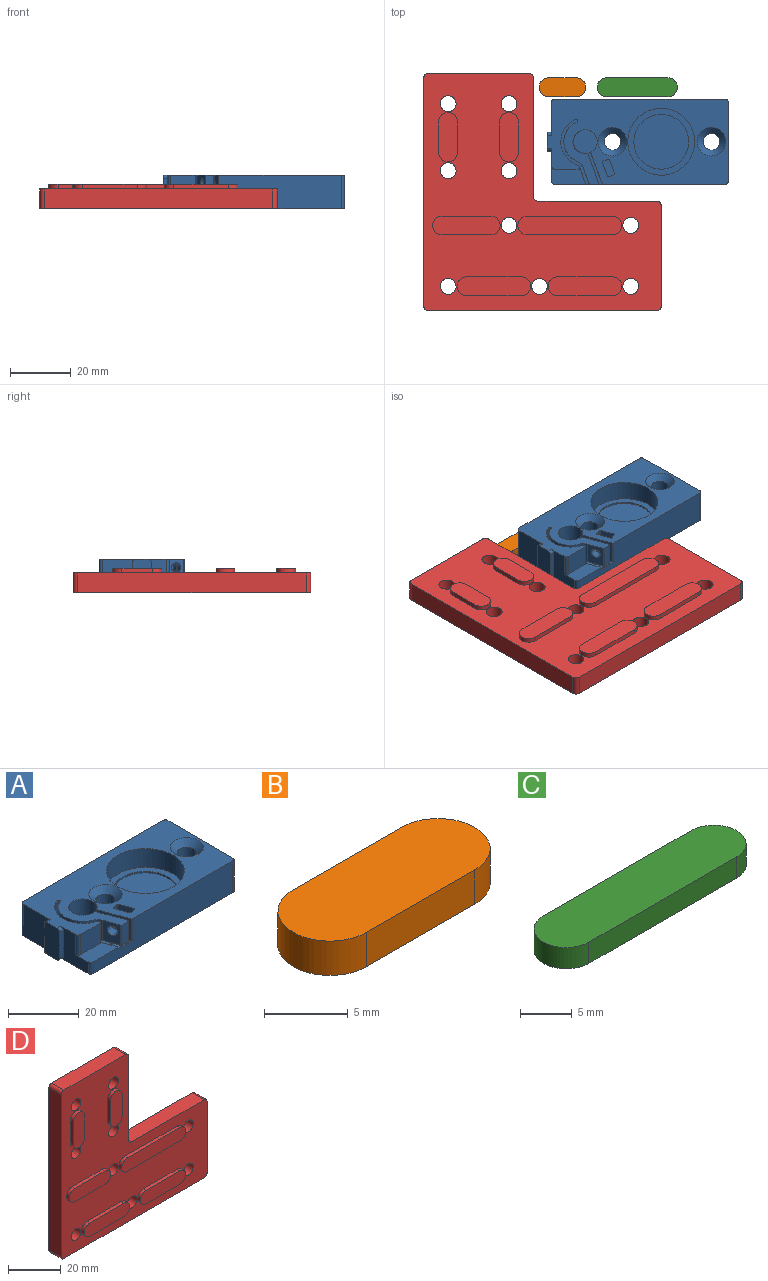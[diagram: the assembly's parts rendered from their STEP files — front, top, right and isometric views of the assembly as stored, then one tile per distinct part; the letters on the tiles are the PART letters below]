
ASSEMBLY  parts=4 mates=3
PART A: 89 faces, bbox 59.5x28x11 mm
  f0: plane 0.33x0.24mm, normal (0,0,-1), area 0mm2, adj f13,f29,f73
  f1: plane 59.5x28mm, normal (0,0,-1), area 1340.5mm2, adj f2,f24,f25,f26,f27,f44,f46,f53
  f2: plane 11x10.9mm, normal (-1,0,0), area 74.3mm2, adj f1,f12,f41,f51,f65,f66,f68,f69
  f3: cylinder r=0.3mm len=7.5mm, axis (0,0,1), area 3.6mm2, adj f4,f12,f21,f43
  f4: cylinder r=8mm len=14.77mm, axis (0,0,1), area 141.2mm2, adj f3,f5,f12,f43
  f5: cylinder r=3mm len=7.5mm, axis (0,0,1), area 13.8mm2, adj f4,f9,f12,f22,f43
  f6: cylinder r=0.3mm len=7.5mm, axis (0,0,1), area 2.7mm2, adj f7,f12,f27,f43
  f7: plane 10.43x7.5mm, normal (-0.94,-0.34,0), area 73.8mm2, adj f6,f8,f12,f29,f39,f42,f43
  f8: cylinder r=3.8mm len=7.37mm, axis (0,0,1), area 6.2mm2, adj f7,f21,f42,f43
  f9: plane 5.07x1.85mm, normal (0.94,0.34,0), area 2.7mm2, adj f5,f10,f22,f41,f43
  f10: cylinder r=0.3mm len=0.5mm, axis (0,0,1), area 0.3mm2, adj f9,f27,f41,f43
  f11: plane 20.85x11.42mm, normal (0,0,-1), area 68.7mm2, adj f13,f14,f15,f16,f17,f18,f19,f20
  f12: plane 59.5x28mm, normal (0,0,1), area 957.2mm2, adj f2,f3,f4,f5,f6,f7,f13,f14
  f13: plane 9.7x7mm, normal (0.94,0.34,0), area 64.2mm2, adj f0,f11,f12,f14,f29,f40
  f14: cylinder r=0.3mm len=7.5mm, axis (0,0,1), area 5mm2, adj f11,f12,f13,f15,f43
  f15: plane 7x2.55mm, normal (0,-1,0), area 17.9mm2, adj f11,f12,f14,f16
  f16: cylinder r=0.3mm len=7mm, axis (0,0,1), area 2.6mm2, adj f11,f12,f15,f17
  f17: plane 7x5.46mm, normal (-0.94,-0.34,0), area 32.7mm2, adj f11,f12,f16,f18,f40
  f18: cylinder r=3mm len=7mm, axis (0,0,1), area 18.1mm2, adj f11,f12,f17,f19
  f19: cylinder r=7mm len=13.03mm, axis (0,0,1), area 117.3mm2, adj f11,f12,f18,f20,f75
  f20: cylinder r=0.3mm len=7mm, axis (0,0,1), area 3.2mm2, adj f11,f12,f19,f21
  f21: plane 7.5x3.66mm, normal (-0.94,-0.34,0), area 4.7mm2, adj f3,f8,f11,f12,f20,f42,f43
  f22: cylinder r=0.3mm len=7mm, axis (0,0,1), area 4.5mm2, adj f5,f9,f12,f23,f41
  f23: plane 8x7mm, normal (0,-1,0), area 56mm2, adj f12,f22,f41,f69
  f24: plane 11x10.9mm, normal (-1,0,0), area 109.3mm2, adj f1,f12,f52,f64,f67,f70
  f25: plane 56x11mm, normal (0,1,0), area 616mm2, adj f1,f12,f70,f71
  f26: plane 26x11mm, normal (1,0,0), area 286mm2, adj f1,f12,f71,f72
  f27: plane 56x11mm, normal (0,-1,0), area 502.1mm2, adj f1,f6,f10,f12,f41,f43,f68,f72
  f28: cylinder r=11mm len=22mm, axis (0,0,1), area 449.2mm2, adj f12,f49
  f29: cylinder r=4mm len=8mm, axis (0,0,1), area 168.9mm2, adj f0,f7,f11,f12,f13,f42
  f30: plane 5.5x4.6mm, normal (-0.94,-0.34,0), area 27mm2, adj f12,f31,f37,f38
  f31: cylinder r=0.3mm len=5.5mm, axis (0,0,1), area 2.6mm2, adj f12,f30,f32,f38
  f32: plane 5.5x1.79mm, normal (-0.34,0.94,0), area 10.4mm2, adj f12,f31,f33,f38
  f33: cylinder r=0.3mm len=5.5mm, axis (0,0,1), area 2.6mm2, adj f12,f32,f34,f38
  f34: plane 5.5x4.6mm, normal (0.94,0.34,0), area 18.9mm2, adj f12,f33,f35,f38,f39
  f35: cylinder r=0.3mm len=5.5mm, axis (0,0,1), area 2.6mm2, adj f12,f34,f36,f38
  f36: plane 5.5x1.79mm, normal (0.34,-0.94,0), area 10.4mm2, adj f12,f35,f37,f38
  f37: cylinder r=0.3mm len=5.5mm, axis (0,0,1), area 2.6mm2, adj f12,f30,f36,f38
  f38: plane 5.85x4.06mm, normal (0,0,1), area 13.7mm2, adj f30,f31,f32,f33,f34,f35,f36,f37
  f39: cylinder r=1.6mm len=3.86mm, axis (0.94,0.34,0), area 25.1mm2, adj f7,f34
  f40: cylinder r=1.6mm len=4.03mm, axis (0.94,0.34,0), area 30.2mm2, adj f13,f17
  f41: plane 11.11x6mm, normal (0,0,1), area 51.6mm2, adj f2,f9,f10,f22,f23,f27,f68,f69
  f42: plane 7.8x7.8mm, normal (0,0,1), area 47.7mm2, adj f7,f8,f21,f29
  f43: plane 21.43x13.84mm, normal (0,0,1), area 108.9mm2, adj f3,f4,f5,f6,f7,f8,f9,f10
  f44: cylinder r=2.75mm len=9.05mm, axis (0,0,1), area 156.4mm2, adj f1,f45
  f45: cone r=2.75mm half-angle=45deg, axis (0,0,1), area 64.5mm2, adj f12,f44
  f46: cylinder r=2.75mm len=9.05mm, axis (0,0,1), area 156.4mm2, adj f1,f47
  f47: cone r=2.75mm half-angle=45deg, axis (0,0,1), area 64.5mm2, adj f12,f46
  f48: cylinder r=9mm len=18mm, axis (0,0,-1), area 28.3mm2, adj f49,f50
  f49: plane 22x22mm, normal (0,0,1), area 125.7mm2, adj f28,f48
  f50: plane 18x18mm, normal (0,0,1), area 254.5mm2, adj f48
  f51: plane 9x1.5mm, normal (0,-1,0), area 13.5mm2, adj f2,f53,f65,f66
  f52: plane 9x1.5mm, normal (0,1,0), area 13.5mm2, adj f24,f53,f64,f67
  f53: plane 11x6.2mm, normal (-1,0,0), area 67.3mm2, adj f1,f12,f51,f52,f64,f65,f66,f67
  f54: cylinder r=3.1mm len=6.2mm, axis (0,0,-1), area 14.6mm2, adj f1,f55,f57,f58
  f55: plane 9.1x1.5mm, normal (0,1,0), area 13.7mm2, adj f1,f54,f56,f58
  f56: cylinder r=3.1mm len=6.2mm, axis (0,0,-1), area 14.6mm2, adj f1,f55,f57,f58
  f57: plane 9.1x1.5mm, normal (0,-1,0), area 13.7mm2, adj f1,f54,f56,f58
  f58: plane 15.3x6.2mm, normal (0,0,-1), area 86.6mm2, adj f54,f55,f56,f57
  f59: cylinder r=3.1mm len=6.2mm, axis (0,0,-1), area 14.6mm2, adj f1,f60,f62,f63
  f60: plane 20.1x1.5mm, normal (0,1,0), area 30.1mm2, adj f1,f59,f61,f63
  f61: cylinder r=3.1mm len=6.2mm, axis (0,0,-1), area 14.6mm2, adj f1,f60,f62,f63
  f62: plane 20.1x1.5mm, normal (0,-1,0), area 30.1mm2, adj f1,f59,f61,f63
  f63: plane 26.3x6.2mm, normal (0,0,-1), area 154.8mm2, adj f59,f60,f61,f62
  f64: cylinder r=1mm len=1.5mm, axis (1,0,0), area 2.4mm2, adj f12,f24,f52,f53
  f65: cylinder r=1mm len=1.5mm, axis (-1,0,0), area 2.4mm2, adj f2,f12,f51,f53
  f66: cylinder r=1mm len=1.5mm, axis (-1,0,0), area 2.4mm2, adj f1,f2,f51,f53
  f67: cylinder r=1mm len=1.5mm, axis (1,0,0), area 2.4mm2, adj f1,f24,f52,f53
  f68: cylinder r=1mm len=4mm, axis (0,0,1), area 6.3mm2, adj f1,f2,f27,f41
  f69: cylinder r=1mm len=7mm, axis (0,0,-1), area 11mm2, adj f2,f12,f23,f41
  f70: cylinder r=1mm len=11mm, axis (0,0,-1), area 17.3mm2, adj f1,f12,f24,f25
  f71: cylinder r=1mm len=11mm, axis (0,0,1), area 17.3mm2, adj f1,f12,f25,f26
  f72: cylinder r=1mm len=11mm, axis (0,0,-1), area 17.3mm2, adj f1,f12,f26,f27
  f73: cylinder r=0.3mm len=0.6mm, axis (0,0,1), area 0.9mm2, adj f0,f11,f43
  f74: cylinder r=0.3mm len=0.6mm, axis (0,0,1), area 0.9mm2, adj f11,f43,f75
  f75: plane 0.12x0.05mm, normal (0,0,1), area 0mm2, adj f19,f74
  f76: cylinder r=0.3mm len=0.6mm, axis (0,0,1), area 0.9mm2, adj f11,f43
  f77: cylinder r=0.3mm len=0.6mm, axis (0,0,1), area 0.9mm2, adj f11,f43
  f78: cylinder r=0.3mm len=0.6mm, axis (0,0,1), area 0.9mm2, adj f11,f43
  f79: cylinder r=0.3mm len=0.6mm, axis (0,0,1), area 0.9mm2, adj f11,f43
  f80: cylinder r=0.3mm len=0.6mm, axis (0,0,1), area 0.9mm2, adj f11,f43
  f81: cylinder r=0.3mm len=0.6mm, axis (0,0,1), area 0.9mm2, adj f11,f43
  f82: cylinder r=0.3mm len=0.6mm, axis (0,0,1), area 0.9mm2, adj f11,f43
  f83: cylinder r=0.3mm len=0.6mm, axis (0,0,1), area 0.9mm2, adj f11,f43
  f84: cylinder r=0.3mm len=0.6mm, axis (0,0,1), area 0.9mm2, adj f11,f43
  f85: cylinder r=0.3mm len=0.6mm, axis (0,0,1), area 0.9mm2, adj f11,f43
  f86: cylinder r=0.3mm len=0.6mm, axis (0,0,1), area 0.9mm2, adj f11,f43
  f87: cylinder r=0.3mm len=0.6mm, axis (0,0,1), area 0.9mm2, adj f11,f43
  f88: cylinder r=0.3mm len=0.6mm, axis (0,0,1), area 0.9mm2, adj f11,f43
PART B: 6 faces, bbox 15.3x6.2x2.5 mm
  f0: cylinder r=3.1mm len=6.2mm, axis (0,0,1), area 24.3mm2, adj f1,f3,f4,f5
  f1: plane 9.1x2.5mm, normal (0,-1,0), area 22.8mm2, adj f0,f2,f4,f5
  f2: cylinder r=3.1mm len=6.2mm, axis (0,0,1), area 24.3mm2, adj f1,f3,f4,f5
  f3: plane 9.1x2.5mm, normal (0,1,0), area 22.8mm2, adj f0,f2,f4,f5
  f4: plane 15.3x6.2mm, normal (0,0,-1), area 86.6mm2, adj f0,f1,f2,f3
  f5: plane 15.3x6.2mm, normal (0,0,1), area 86.6mm2, adj f0,f1,f2,f3
PART C: 6 faces, bbox 26.3x6.2x2.5 mm
  f0: cylinder r=3.1mm len=6.2mm, axis (0,0,1), area 24.3mm2, adj f1,f3,f4,f5
  f1: plane 20.1x2.5mm, normal (0,-1,0), area 50.3mm2, adj f0,f2,f4,f5
  f2: cylinder r=3.1mm len=6.2mm, axis (0,0,1), area 24.3mm2, adj f1,f3,f4,f5
  f3: plane 20.1x2.5mm, normal (0,1,0), area 50.3mm2, adj f0,f2,f4,f5
  f4: plane 26.3x6.2mm, normal (0,0,-1), area 154.8mm2, adj f0,f1,f2,f3
  f5: plane 26.3x6.2mm, normal (0,0,1), area 154.8mm2, adj f0,f1,f2,f3
PART D: 53 faces, bbox 78x8x78 mm
  f0: plane 39x6.5mm, normal (0,0,1), area 253.5mm2, adj f6,f7,f47,f52
  f1: plane 39x6.5mm, normal (1,0,0), area 253.5mm2, adj f6,f7,f47,f48
  f2: plane 33x6.5mm, normal (0,0,1), area 214.5mm2, adj f6,f7,f48,f49
  f3: plane 75x6.5mm, normal (-1,0,0), area 487.5mm2, adj f6,f7,f49,f50
  f4: plane 75x6.5mm, normal (0,0,-1), area 487.5mm2, adj f6,f7,f50,f51
  f5: plane 33x6.5mm, normal (1,0,0), area 214.5mm2, adj f6,f7,f51,f52
  f6: plane 78x78mm, normal (0,-1,0), area 3325.8mm2, adj f0,f1,f2,f3,f4,f5,f8,f9
  f7: plane 78x78mm, normal (0,1,0), area 4126.9mm2, adj f0,f1,f2,f3,f4,f5,f8,f9
  f8: cylinder r=2.6mm len=6.5mm, axis (0,1,0), area 106.2mm2, adj f6,f7
  f9: cylinder r=2.6mm len=6.5mm, axis (0,1,0), area 106.2mm2, adj f6,f7
  f10: cylinder r=2.6mm len=6.5mm, axis (0,1,0), area 106.2mm2, adj f6,f7
  f11: cylinder r=2.6mm len=6.5mm, axis (0,1,0), area 106.2mm2, adj f6,f7
  f12: cylinder r=2.6mm len=6.5mm, axis (0,1,0), area 106.2mm2, adj f6,f7
  f13: cylinder r=2.6mm len=6.5mm, axis (0,1,0), area 106.2mm2, adj f6,f7
  f14: cylinder r=2.6mm len=6.5mm, axis (0,1,0), area 106.2mm2, adj f6,f7
  f15: cylinder r=2.6mm len=6.5mm, axis (0,1,0), area 106.2mm2, adj f6,f7
  f16: cylinder r=2.6mm len=6.5mm, axis (0,1,0), area 106.2mm2, adj f6,f7
  f17: cylinder r=3.1mm len=6.2mm, axis (0,1,0), area 14.6mm2, adj f6,f18,f20,f21
  f18: plane 28x1.5mm, normal (0,0,1), area 42mm2, adj f6,f17,f19,f21
  f19: cylinder r=3.1mm len=6.2mm, axis (0,1,0), area 14.6mm2, adj f6,f18,f20,f21
  f20: plane 28x1.5mm, normal (0,0,-1), area 42mm2, adj f6,f17,f19,f21
  f21: plane 34.2x6.2mm, normal (0,-1,0), area 203.8mm2, adj f17,f18,f19,f20
  f22: cylinder r=3.1mm len=6.2mm, axis (0,1,0), area 14.6mm2, adj f6,f23,f25,f26
  f23: plane 18x1.5mm, normal (0,0,1), area 27mm2, adj f6,f22,f24,f26
  f24: cylinder r=3.1mm len=6.2mm, axis (0,1,0), area 14.6mm2, adj f6,f23,f25,f26
  f25: plane 18x1.5mm, normal (0,0,-1), area 27mm2, adj f6,f22,f24,f26
  f26: plane 24.2x6.2mm, normal (0,-1,0), area 141.8mm2, adj f22,f23,f24,f25
  f27: cylinder r=3.1mm len=6.2mm, axis (0,1,0), area 14.6mm2, adj f6,f28,f30,f31
  f28: plane 18x1.5mm, normal (0,0,1), area 27mm2, adj f6,f27,f29,f31
  f29: cylinder r=3.1mm len=6.2mm, axis (0,1,0), area 14.6mm2, adj f6,f28,f30,f31
  f30: plane 18x1.5mm, normal (0,0,-1), area 27mm2, adj f6,f27,f29,f31
  f31: plane 24.2x6.2mm, normal (0,-1,0), area 141.8mm2, adj f27,f28,f29,f30
  f32: cylinder r=3.1mm len=6.2mm, axis (0,1,0), area 14.6mm2, adj f6,f33,f35,f36
  f33: plane 10x1.5mm, normal (1,0,0), area 15mm2, adj f6,f32,f34,f36
  f34: cylinder r=3.1mm len=6.2mm, axis (0,1,0), area 14.6mm2, adj f6,f33,f35,f36
  f35: plane 10x1.5mm, normal (-1,0,0), area 15mm2, adj f6,f32,f34,f36
  f36: plane 16.2x6.2mm, normal (0,-1,0), area 92.2mm2, adj f32,f33,f34,f35
  f37: cylinder r=3.1mm len=6.2mm, axis (0,1,0), area 14.6mm2, adj f6,f38,f40,f41
  f38: plane 10x1.5mm, normal (1,0,0), area 15mm2, adj f6,f37,f39,f41
  f39: cylinder r=3.1mm len=6.2mm, axis (0,1,0), area 14.6mm2, adj f6,f38,f40,f41
  f40: plane 10x1.5mm, normal (-1,0,0), area 15mm2, adj f6,f37,f39,f41
  f41: plane 16.2x6.2mm, normal (0,-1,0), area 92.2mm2, adj f37,f38,f39,f40
  f42: cylinder r=3.1mm len=6.2mm, axis (0,1,0), area 14.6mm2, adj f6,f43,f45,f46
  f43: plane 16x1.5mm, normal (0,0,1), area 24mm2, adj f6,f42,f44,f46
  f44: cylinder r=3.1mm len=6.2mm, axis (0,1,0), area 14.6mm2, adj f6,f43,f45,f46
  f45: plane 16x1.5mm, normal (0,0,-1), area 24mm2, adj f6,f42,f44,f46
  f46: plane 22.2x6.2mm, normal (0,-1,0), area 129.4mm2, adj f42,f43,f44,f45
  f47: cylinder r=1.5mm len=6.5mm, axis (0,-1,0), area 15.3mm2, adj f0,f1,f6,f7
  f48: cylinder r=1.5mm len=6.5mm, axis (0,1,0), area 15.3mm2, adj f1,f2,f6,f7
  f49: cylinder r=1.5mm len=6.5mm, axis (0,1,0), area 15.3mm2, adj f2,f3,f6,f7
  f50: cylinder r=1.5mm len=6.5mm, axis (0,1,0), area 15.3mm2, adj f3,f4,f6,f7
  f51: cylinder r=1.5mm len=6.5mm, axis (0,1,0), area 15.3mm2, adj f4,f5,f6,f7
  f52: cylinder r=1.5mm len=6.5mm, axis (0,1,0), area 15.3mm2, adj f0,f5,f6,f7
PLACE A t=(19.56,-82.5,11)mm
PLACE B t=(13.86,-64.6,17.5)mm
PLACE C t=(11.46,-64.6,17.5)mm
PLACE D rot(axis=(-1,0,0),90deg) t=(8,8,140)mm
MATE fastened C.f4 <-> B.f4  axis (0,0,-1) through (32.1,48.5,0)mm
MATE fastened A.f1 <-> D.f7  axis (0,0,-1) through (14,40.5,0)mm
MATE fastened B.f4 <-> D.f7  axis (0,0,-1) through (13,48.5,0)mm
